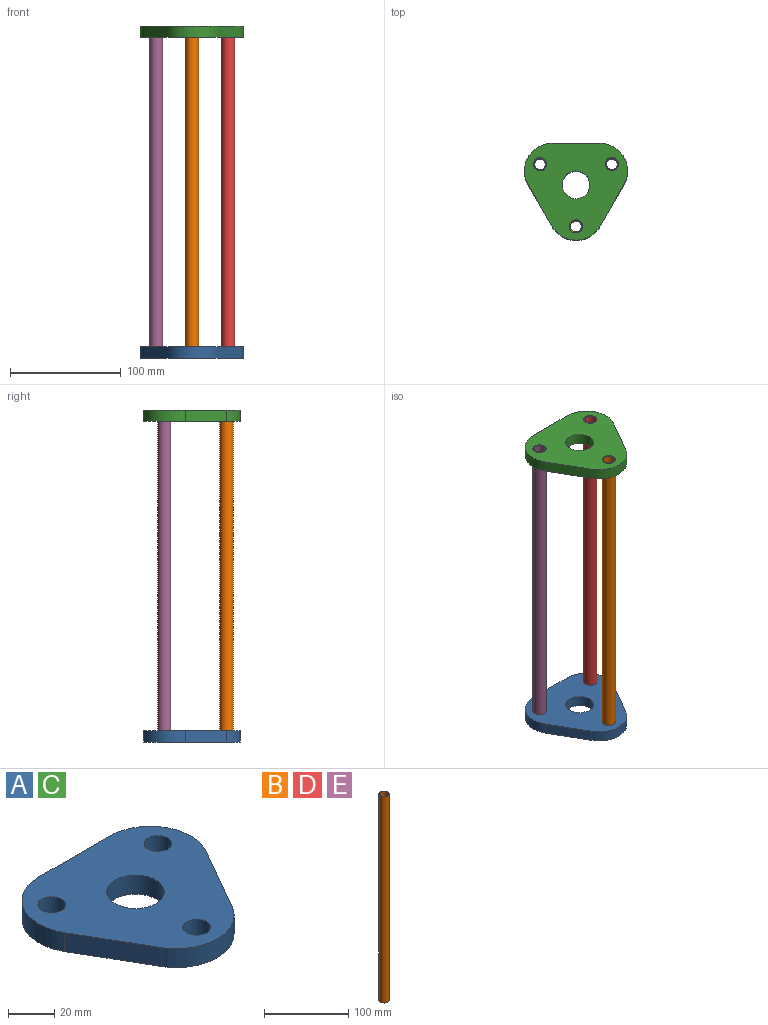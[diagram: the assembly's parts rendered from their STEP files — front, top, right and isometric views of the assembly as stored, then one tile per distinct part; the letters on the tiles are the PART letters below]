
ASSEMBLY  parts=5 mates=4
PART A: 12 faces, bbox 93.3x87.5x10 mm
  f0: plane 43.3x10mm, normal (0,1,0), area 433mm2, adj f1,f8,f10,f11
  f1: cylinder r=25mm len=37.5mm, axis (0,0,-1), area 523.6mm2, adj f0,f2,f10,f11
  f2: plane 37.5x21.65mm, normal (-0.87,-0.5,0), area 433mm2, adj f1,f3,f10,f11
  f3: cylinder r=25mm len=43.3mm, axis (0,0,-1), area 523.6mm2, adj f2,f4,f10,f11
  f4: plane 37.5x21.65mm, normal (0.87,-0.5,0), area 433mm2, adj f3,f8,f10,f11
  f5: cylinder r=6mm len=12mm, axis (0,0,-1), area 377mm2, adj f10,f11
  f6: cylinder r=6mm len=12mm, axis (0,0,-1), area 377mm2, adj f10,f11
  f7: cylinder r=6mm len=12mm, axis (0,0,-1), area 377mm2, adj f10,f11
  f8: cylinder r=25mm len=37.5mm, axis (0,0,-1), area 523.6mm2, adj f0,f4,f10,f11
  f9: cylinder r=12.5mm len=25mm, axis (0,0,-1), area 785.4mm2, adj f10,f11
  f10: plane 93.3x87.5mm, normal (0,0,1), area 5192.8mm2, adj f0,f1,f2,f3,f4,f5,f6,f7
  f11: plane 93.3x87.5mm, normal (0,0,-1), area 5192.8mm2, adj f0,f1,f2,f3,f4,f5,f6,f7
PART B: 4 faces, bbox 12x12x300 mm
  f0: cylinder r=5mm len=300mm, axis (0,0,-1), area 9424.8mm2, adj f2,f3
  f1: cylinder r=6mm len=300mm, axis (0,0,-1), area 11309.7mm2, adj f2,f3
  f2: plane 12x12mm, normal (0,0,1), area 34.6mm2, adj f0,f1
  f3: plane 12x12mm, normal (0,0,-1), area 34.6mm2, adj f0,f1
PART C: same geometry as A
PART D: same geometry as B
PART E: same geometry as B
PLACE A t=(-27.58,50.78,-127.87)mm
PLACE B t=(-27.58,13.28,-127.87)mm
PLACE C t=(-27.58,50.78,162.13)mm
PLACE D t=(4.9,69.53,-127.87)mm
PLACE E t=(-60.06,69.53,-127.87)mm
MATE fastened E.f1 <-> A.f5  axis (0,0,-1) through (-60.06,69.53,-127.87)mm
MATE fastened D.f1 <-> A.f6  axis (0,0,-1) through (4.9,69.53,-127.87)mm
MATE fastened C.f2 <-> A.f2  axis (-0.87,-0.5,0) through (-60.06,32.03,167.13)mm
MATE fastened A.f7 <-> B.f1  axis (0,0,-1) through (-27.58,13.28,-127.87)mm
